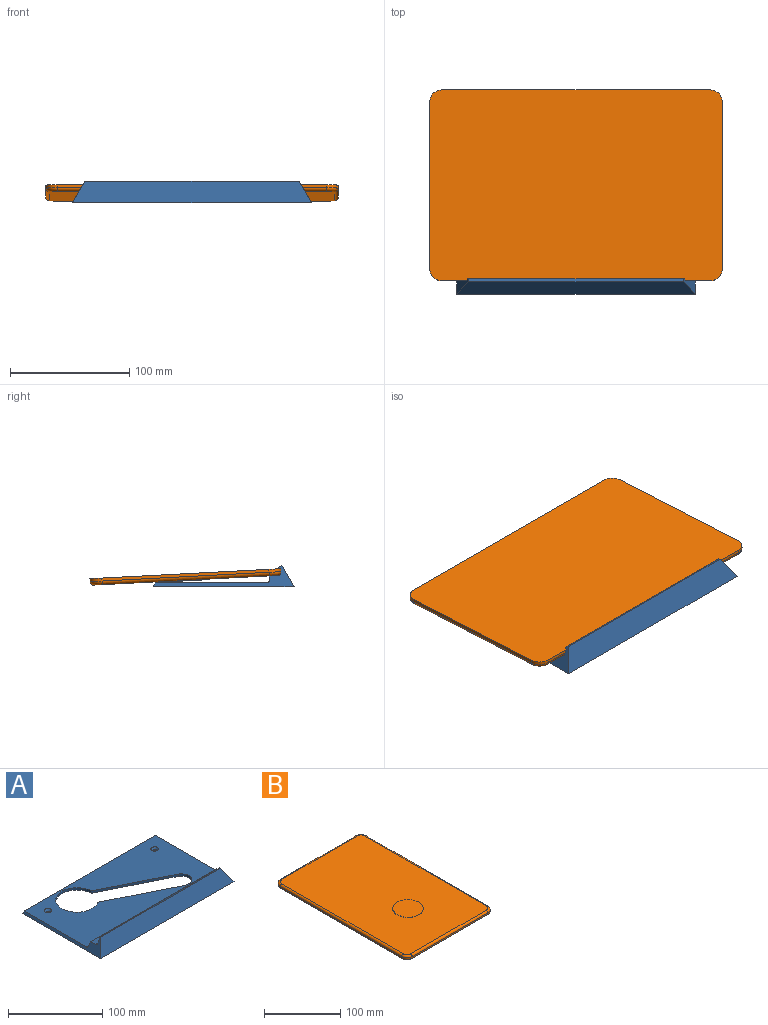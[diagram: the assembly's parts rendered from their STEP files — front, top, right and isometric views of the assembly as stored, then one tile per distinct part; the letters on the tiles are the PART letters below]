
ASSEMBLY  parts=2 mates=1
PART A: 21 faces, bbox 200x118x17.6 mm
  f0: plane 196.54x93.51mm, normal (0,0,1), area 14402.3mm2, adj f8,f9,f12,f13,f14,f15,f17,f18
  f1: plane 200x118mm, normal (0,0,-1), area 19700.4mm2, adj f2,f8,f9,f10,f11,f12,f17,f18
  f2: plane 200x17.65mm, normal (0,-0.87,0.5), area 3867.8mm2, adj f1,f7,f8,f9
  f3: plane 194.23x3.89mm, normal (0,1,0), area 746.5mm2, adj f4,f8,f9,f15
  f4: plane 189.74x7.91mm, normal (0,0.05,1), area 1500.9mm2, adj f3,f8,f9,f16
  f5: plane 186.83x3.6mm, normal (0,1,-0.05), area 665.1mm2, adj f6,f8,f9,f16
  f6: plane 182.68x1.64mm, normal (0,0.57,-0.82), area 364mm2, adj f5,f7,f8,f9
  f7: plane 181.36x2.6mm, normal (0,0.5,0.87), area 541.5mm2, adj f2,f6,f8,f9
  f8: plane 118x17.65mm, normal (-0.87,0,0.5), area 561.4mm2, adj f0,f1,f2,f3,f4,f5,f6,f7
  f9: plane 118x17.65mm, normal (0.87,0,0.5), area 561.4mm2, adj f0,f1,f2,f3,f4,f5,f6,f7
  f10: cylinder r=2mm len=4mm, axis (0,0,-1), area 12.6mm2, adj f1,f14
  f11: cylinder r=2mm len=4mm, axis (0,0,-1), area 12.6mm2, adj f1,f13
  f12: plane 200x3mm, normal (0,0.87,0.5), area 686.8mm2, adj f0,f1,f8,f9
  f13: cone r=2mm half-angle=45deg, axis (0,0,1), area 53.3mm2, adj f0,f11
  f14: cone r=2mm half-angle=45deg, axis (0,0,1), area 53.3mm2, adj f0,f10
  f15: cylinder r=2mm len=196.54mm, axis (1,0,0), area 614.8mm2, adj f0,f3,f8,f9
  f16: cylinder r=2mm len=189.26mm, axis (-1,0,0), area 591.7mm2, adj f4,f5,f8,f9
  f17: cylinder r=11mm len=20.85mm, axis (0,0,-1), area 103.7mm2, adj f0,f1,f18,f20
  f18: plane 86.93x43.3mm, normal (-0.45,-0.9,0), area 291.4mm2, adj f0,f1,f17,f19
  f19: cylinder r=22.5mm len=45mm, axis (0,0,-1), area 355.2mm2, adj f0,f1,f18,f20
  f20: plane 86.93x43.3mm, normal (0.45,0.9,0), area 291.4mm2, adj f0,f1,f17,f19
PART B: 20 faces, bbox 161.6x246.6x6 mm
  f0: plane 239x154mm, normal (0,0,1), area 35507.3mm2, adj f6,f7,f8,f9,f11,f13,f15,f17
  f1: plane 140x2.5mm, normal (0,1,0), area 350mm2, adj f5,f6,f14,f16
  f2: plane 225x2.5mm, normal (-1,0,0), area 562.5mm2, adj f5,f7,f12,f14
  f3: plane 140x2.5mm, normal (0,-1,0), area 350mm2, adj f5,f9,f10,f12
  f4: plane 225x2.5mm, normal (1,0,0), area 562.5mm2, adj f5,f8,f10,f16
  f5: plane 245x160mm, normal (0,0,-1), area 39114.2mm2, adj f1,f2,f3,f4,f10,f12,f14,f16
  f6: cylinder r=3mm len=140mm, axis (1,0,0), area 659.7mm2, adj f0,f1,f15,f17
  f7: cylinder r=3mm len=225mm, axis (0,1,0), area 1060.3mm2, adj f0,f2,f13,f15
  f8: cylinder r=3mm len=225mm, axis (0,-1,0), area 1060.3mm2, adj f0,f4,f11,f17
  f9: cylinder r=3mm len=140mm, axis (-1,0,0), area 659.7mm2, adj f0,f3,f11,f13
  f10: cylinder r=10mm len=10mm, axis (0,0,1), area 39.3mm2, adj f3,f4,f5,f11
  f11: torus R=7mm, axis (0,0,1), area 66mm2, adj f0,f8,f9,f10
  f12: cylinder r=10mm len=10mm, axis (0,0,-1), area 39.3mm2, adj f2,f3,f5,f13
  f13: torus R=7mm, axis (0,0,1), area 66mm2, adj f0,f7,f9,f12
  f14: cylinder r=10mm len=10mm, axis (0,0,1), area 39.3mm2, adj f1,f2,f5,f15
  f15: torus R=7mm, axis (0,0,1), area 66mm2, adj f0,f6,f7,f14
  f16: cylinder r=10mm len=10mm, axis (0,0,-1), area 39.3mm2, adj f1,f4,f5,f17
  f17: torus R=7mm, axis (0,0,1), area 66mm2, adj f0,f6,f8,f16
  f18: cylinder r=20mm len=40mm, axis (0,0,-1), area 62.8mm2, adj f0,f19
  f19: plane 40x40mm, normal (0,0,1), area 1256.6mm2, adj f18
PLACE A t=(-81.43,11.64,17.32)mm
PLACE B rot(axis=(0.71,0.71,-0.02),177.9deg) t=(-81.43,43.68,28.08)mm
MATE fastened B.f2 <-> A.f5  axis (0,-1,0.05) through (-81.43,-36.28,31.02)mm
